# Revit family: KingswayGroup_DrStps_Anti-LigatureExtendedLargeRubberDoorStopWallMountedOnBackPlate
name_source: partatom
category: Specialty Equipment
units: mm (PartAtom-declared; Revit-internal decimal feet)

## family parameters
Always vertical = Yes
Cut with Voids When Loaded = No
Part Type = Normal
Room Calculation Point = No
Round Connector Dimension = Use Diameter
Shared = No
Work Plane-Based = No

## types (1)
- KingswayGroup_DrStps_Anti-LigatureExtendedLargeRubberDoorStopWallMountedOnBackPlate
    AssetType = Fixed
    BIMObjectName = KingswayGroup_DoorStops_Anti-LigatureExtendedLargeRubberDoorStopWallMountedOnBackPlate
    Category = Pr_30_36_33_24:Door stops
    Color = For full range of available finishes and colours, contact Kingsway Group
    Default Elevation = 0 mm  [stored 0 ft]
    Description = Extended Rubber Wall Mounted Door Stop on Back Plate
    DurationUnit = year
    Features = The door stop features a secure back plate and a large high-pressured domed rubber stop, suitable for use on walls and doors in challenging environments. The extended rubber stop prevents breakages by allowing the solid portion of the door to take the impact when thrust open.
    Finish = For full range of available finishes and colours, contact Kingsway Group
    IfcExportAs = IfcDiscreteAccessoryType
    IfcExportType = USERDEFINED
    Manufacturer = Kingsway Group
    ManufacturerName = Kingsway Group
    ManufacturerURL = https://kingswaygroupglobal.com
    Material = Stainless Steel, Rubber
    Model = KG186
    ModelNumber = KG186
    ModelReference = Anti-Ligature Extended Large Rubber Door Stop Wall Mounted On Back Plate
    Name = DoorStops_Anti-LigatureExtendedLargeRubberDoorStopWallMountedOnBackPlate_KG186_KingswayGroup
    NominalHeight = 79 mm
    NominalLength = 114 mm  [stored 0.374016 ft]
    NominalWidth = 114 mm  [stored 0.374016 ft]
    PlateMaterial = NBS_Concept
    ProductInformation = https://kingswaygroupglobal.com
    RubberMaterial = NBS_Concept
    Size = 114 x 79 x 114 mm
    URL = https://kingswaygroupglobal.com
    Uniclass2015Code = Pr_30_36_33_24
    Uniclass2015Title = Door stops
    Uniclass2015Version = Products v1.36
    Version = 1
    WarrantyDescription = 5-Year Guarantee *For faulty manufacture and not for damage
    WarrantyDurationParts = 5
    WarrantyDurationUnit = year

note: [stored X ft] marks values corroborated as IEEE doubles in the binary element streams (Revit-internal decimal feet)

## geometry (parser evidence)
native form markers: Sweep x3
no freeform markers — native parametric forms only
